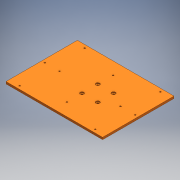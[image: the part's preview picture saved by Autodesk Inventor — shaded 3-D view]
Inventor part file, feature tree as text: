
AUTODESK INVENTOR PART (.ipt)
format: ipt  version: 2016 (Build 200138000, 138)  size: 178,688 bytes
history: native  units: mm
features: sketch x4, extrude x2, hole x2, mirror x2
ambient origin geometry x8: Origin, YZ Plane, XZ Plane, XY Plane, X Axis, Y Axis, Z Axis, Center Point
bodies: Solid1 (feature_tree)
feature tree (10):
  extrude  "baseExtrusion"  Depth=85.05mm
  hole  "zStageM6MountingHoles"  [1 undecoded]
  extrude  "excessExtrusion"  Depth=10.0mm
  hole  "Hole4"  [1 undecoded]
  mirror  "Mirror7"
  mirror  "Mirror8"
  sketch  "Sketch1"  dims[d0=170.1mm d1=85.05mm]
  sketch  "Sketch2"  dims[d2=109.4mm d3=54.7mm]
  sketch  "Sketch5"  dims[d4=10.0mm d5=0.0mm d6=75.0mm]
  sketch  "Sketch7"  dims[d7=75.0mm d9=37.5mm d10=6.6mm d11=6.0mm d12=18.0mm d13=4.8mm d14=90.0deg d15=8.0mm d16=20.594885mm d17=10.6mm d33=10.0mm d34=0.0mm d44=340.0mm d45=170.0mm d46=460.0mm d47=230.0mm d48=15.0mm d50=15.0mm d51=85.0mm d53=6.6mm d54=6.0mm d55=18.0mm d56=4.8mm d57=90.0deg d58=8.0mm d59=20.594885mm d60=50.0mm d61=60.0mm]
note: 2 required parameter values undecoded (feature->parameter linkage not recoverable at this tier; creation-order binding heuristic only, values carry confidence <= 0.55)
